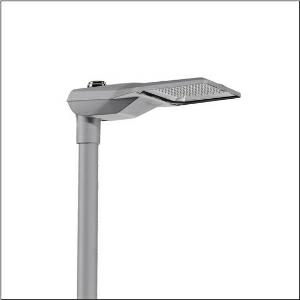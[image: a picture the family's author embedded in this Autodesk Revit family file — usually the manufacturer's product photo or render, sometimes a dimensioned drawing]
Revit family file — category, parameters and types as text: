
# Revit family: streetlight_sl_21_midi___st1_0a_5xe7d47n08nb_e9e4
name_source: partatom
category: Lighting Fixtures
units: mm (PartAtom-declared; Revit-internal decimal feet)

## family parameters
Cut with Voids When Loaded = No
Host = Face
Light Source = No
Part Type = Normal
Room Calculation Point = No
Round Connector Dimension = Use Diameter
Shared = No

## types (1)
- --- (1 x LED, 23710 lm, 151.2 W, 4000K)
    Apparent Load = 151 VA
    CIE Flux Codes = 40 73 97 100 100
    Color Rendering = 70
    Color Temperature = 4000K
    Default Elevation = 1800 mm
    Description = Streetlight SL 21 midi, mast luminaire, primary light control with lens, of PMMA, primary optical cover: cover, of toughened safety glass, transparent, light distribution: ST1.0a, light emission: direct distribution, primary light characteristic: asymmetric, installation type: side-entry, LED, 3G 2.5mm², High Power LED, rated luminous flux: 23.710lm, luminous efficacy: 157lm/W, light colour: 740, colour temperature: 4000K, control gear: NEMA (7pin), control: overheat protection, pre-setting: linear dimming characteristic, constant luminous flux control, time-dependent luminous flux control, flexible luminous flux parameterisation, mains connection: 220..240V, AC, 50/60Hz, connection cable pre-assembled, cable length: 12,5m, wiring characteristics: H05VV-F, start of lifetime: 151W, end of service life: 157W, reduction: 70W, luminaire housing, of diecast aluminium (EN AC-44300), powder-coated, SITECO metallic grey (DB 702S), corrosivity category C5 high according to DIN EN ISO 12944, multi-level sealing system, sealing non-destructively replaceable, inclination adjustable: 0°, 5°, 10°, 15°, length: 644mm, width: 335mm, height: 110mm, spigot size: 42mm (side-entry), mounting height: 4..8m, protection rating (complete): IP66, insulation class (complete): insulation class I (protective earthing), certification: CE, ENEC, ENEC+, VDE, impact resistance: IK10, permissible operating ambient temperature for outdoor applications: -40..+50°C, standard-compliant lighting for roads and squares, packaging unit: 1 piece

Light Distribution: ST1.0a
    Height = 111 mm
    Lamp = 1 x LED
    Lamp Light Flux = 23710 lm
    Lamp Power = 151.2 W
    Lamp count = 1
    Length = 644 mm
    Luminous efficacy = 157 lm/W
    Manufacturer = Siteco
    ModVariant = No
    Model = 5XE7D47N08NB
    Number of Poles = 1
    OnlyDefault = Yes
    Power Factor = 1
    Product Name = Streetlight SL 21 midi | ST1.0a
    Product group = mast luminaire | pylon top
    ProductGroupID = 6100
    Protection Class = Protection class I
    Protection Degree = IP 66
    RLX_Detail_Level = 1
    RLX_Emergency_Light_Flux = 0 lm
    RLX_Emergency_Type = 0
    RLX_Emergency_Type_DB = No
    RlxData = <blob elided: 26661 chars, md5=2a1eb26e>
    Socket = socket
    Standby Power = 0 W
    System Light Flux = 23710 lm
    System Power = 151 W
    Type Comments = factory setting: luminous flux: 100 % | dim-lin: 254 | 802 mA
    Type Image = l_1294377.jpg
    URL = http://relux.com
    VarID = @adj_134623
    Voltage = 0 V
    Weight = 0.00 kg
    Width = 336 mm

## geometry (parser evidence)
native form markers: Blend x4, Sweep x11
no freeform markers — native parametric forms only
